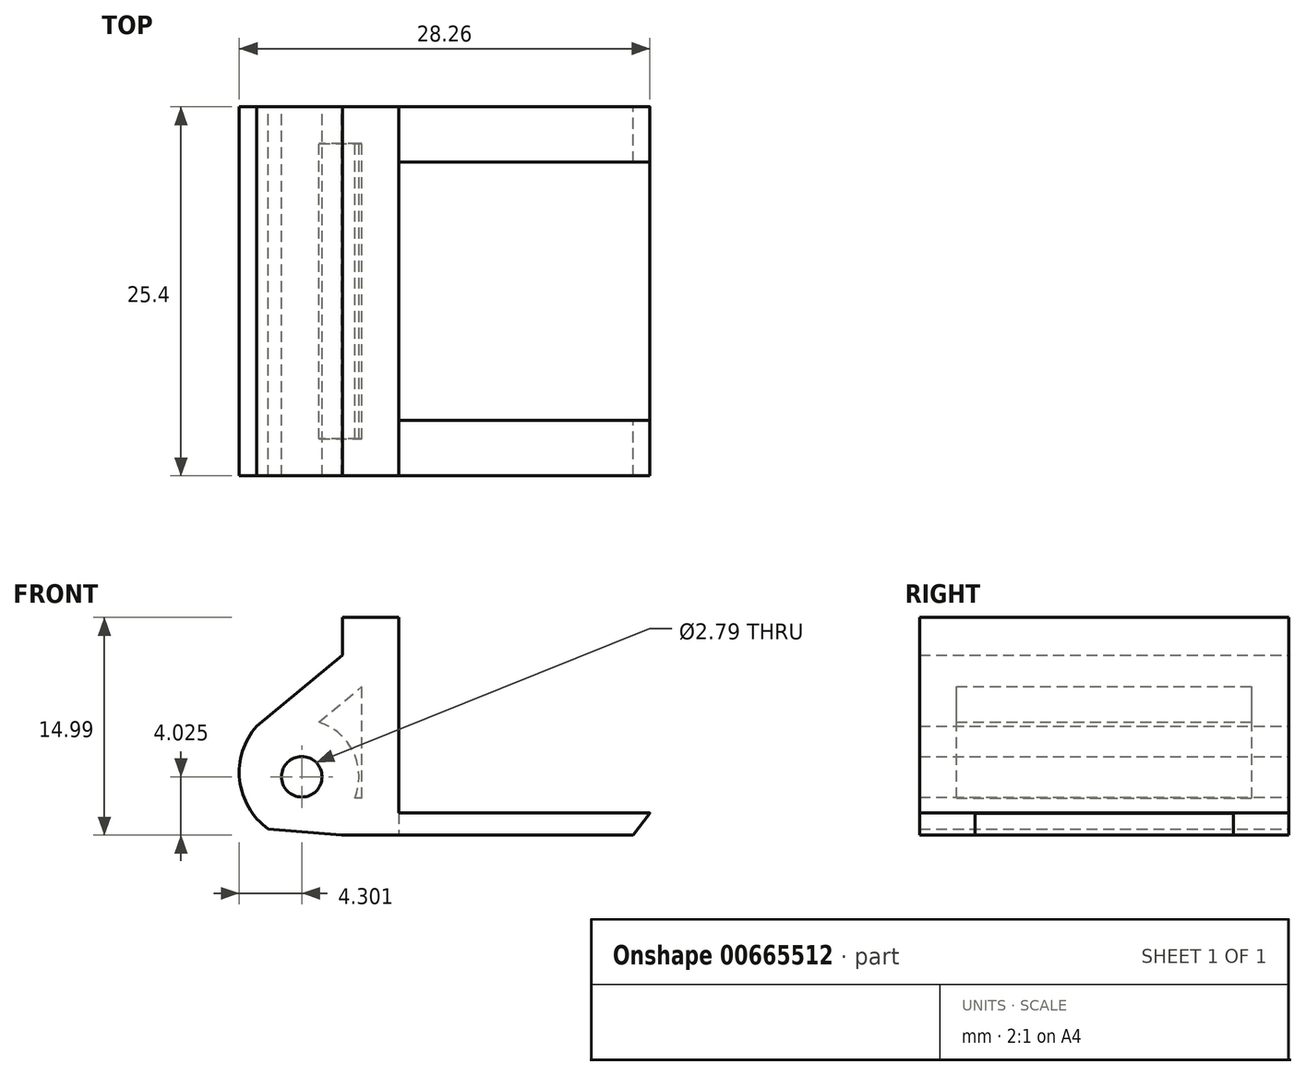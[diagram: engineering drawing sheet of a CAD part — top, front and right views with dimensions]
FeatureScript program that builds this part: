
annotation { "Feature Type Name" : "Feature", "Feature Type Description" : "" }
export const myFeature = defineFeature(function(context is Context, id is Id, definition is map)
    precondition{}
    {
        {
            var Q0;
            Q0=qCreatedBy(makeId("Front.planeOp"),FACE);
            var sketch = newSketch(context, id + "F0", { "sketchPlane" : qUnion([Q0])});
            skLineSegment(sketch, "E0", {"start": v(-37.9, 5.13) * mm, "end": v(-20.64, 5.13) * mm});
            skLineSegment(sketch, "E1", {"start": v(-20.64, 5.13) * mm, "end": v(-21.78, 3.61) * mm});
            skLineSegment(sketch, "E2", {"start": v(-21.78, 3.61) * mm, "end": v(-37.9, 3.61) * mm});
            skPoint(sketch, "E3.visualSharp", {"position": v(-20.63, 5.13) * mm});
            skArc(sketch, "E3.filletArc", {"start": v(-20.64, 5.13) * mm, "mid": v(-20.64, 5.13) * mm, "end": v(-20.64, 5.13) * mm});
            skLineSegment(sketch, "E4.bottom", {"start": v(-37.9, 3.61) * mm, "end": v(-41.84, 3.61) * mm});
            skLineSegment(sketch, "E4.top", {"start": v(-37.9, 18.6) * mm, "end": v(-41.8, 18.6) * mm});
            skLineSegment(sketch, "E4.left", {"start": v(-37.9, 3.61) * mm, "end": v(-37.9, 18.6) * mm});
            skLineSegment(sketch, "E4.right", {"start": v(-41.8, 3.61) * mm, "end": v(-41.8, 18.6) * mm});
            skLineSegment(sketch, "E5", {"start": v(-41.84, 3.61) * mm, "end": v(-46.9, 4.04) * mm});
            skArc(sketch, "E6", {"start": v(-47.7, 11.12) * mm, "mid": v(-48.87, 7.4) * mm, "end": v(-46.9, 4.04) * mm});
            skLineSegment(sketch, "E7", {"start": v(-47.7, 11.12) * mm, "end": v(-41.8, 16) * mm});
            skCircle(sketch, "E8", {"center": v(-44.6, 7.63) * mm, "radius": 1.4 * mm});
            skSolve(sketch);
        }
        {
            var Q0;
            {var subQ0=sQuery(id+"F0.wireOp",EDGE,"E5");Q0=makeQuery(id+"F0.imprint","IMPRINT",FACE,{"disambiguationData":[TD([[makeQuery(id+"F0.imprint","IMPRINT",EDGE,{"derivedFrom":subQ0}),-1.0]])]});}
            var Q1;
            {var subQ2=sQuery(id+"F0.wireOp",EDGE,"E4.top");Q1=makeQuery(id+"F0.imprint","IMPRINT",FACE,{"disambiguationData":[TD([[makeQuery(id+"F0.imprint","IMPRINT",EDGE,{"derivedFrom":subQ2}),1.0]])]});}
            var Q2;
            {var subQ1=sQuery(id+"F0.wireOp",EDGE,"E0");Q2=makeQuery(id+"F0.imprint","IMPRINT",FACE,{"disambiguationData":[TD([[makeQuery(id+"F0.imprint","IMPRINT",EDGE,{"derivedFrom":subQ1}),-1.0]])]});}
            extrude(context, id + "F1", {"entities" : qUnion([Q0, Q1, Q2]), "depth" : 25.4 * mm, "offsetDistance" : 25.4 * mm});
        }
        {
            var Q0;
            Q0=makeQuery(id+"F1.opExtrude","SWEPT_FACE",FACE,{"disambiguationData":[OSD([sQuery(id+"F0.wireOp",EDGE,"E0")])]});
            shell(context, id + "F2", {"entities" : qUnion([Q0]), "thickness" : 2.54 * mm});
        }
        {
            var Q0;
            Q0=makeQuery(id+"F1.opExtrude","SWEPT_FACE",FACE,{"disambiguationData":[OSD([sQuery(id+"F0.wireOp",EDGE,"E0")])]});
            var sketch = newSketch(context, id + "F3", { "sketchPlane" : qUnion([Q0])});
            skLineSegment(sketch, "E9.bottom", {"start": v(-37.9, -3.81) * mm, "end": v(-20.13, -3.81) * mm});
            skLineSegment(sketch, "E9.top", {"start": v(-37.9, -21.59) * mm, "end": v(-20.13, -21.59) * mm});
            skLineSegment(sketch, "E9.left", {"start": v(-37.9, -3.81) * mm, "end": v(-37.9, -21.59) * mm});
            skLineSegment(sketch, "E9.right", {"start": v(-20.13, -3.81) * mm, "end": v(-20.13, -21.59) * mm});
            skSolve(sketch);
        }
        {
            var Q0;
            {var subQ0=sQuery(id+"F3.wireOp",EDGE,"E9.left");Q0=makeQuery(id+"F3.imprint","IMPRINT",FACE,{"disambiguationData":[TD([[makeQuery(id+"F3.imprint","IMPRINT",EDGE,{"derivedFrom":subQ0}),1.0]])]});}
            extrude(context, id + "F4", {"entities" : qUnion([Q0]), "operationType" : NewBodyOperationType.REMOVE, "oppositeDirection" : true, "depth" : 25.4 * mm, "offsetDistance" : 25.4 * mm});
        }
    });
